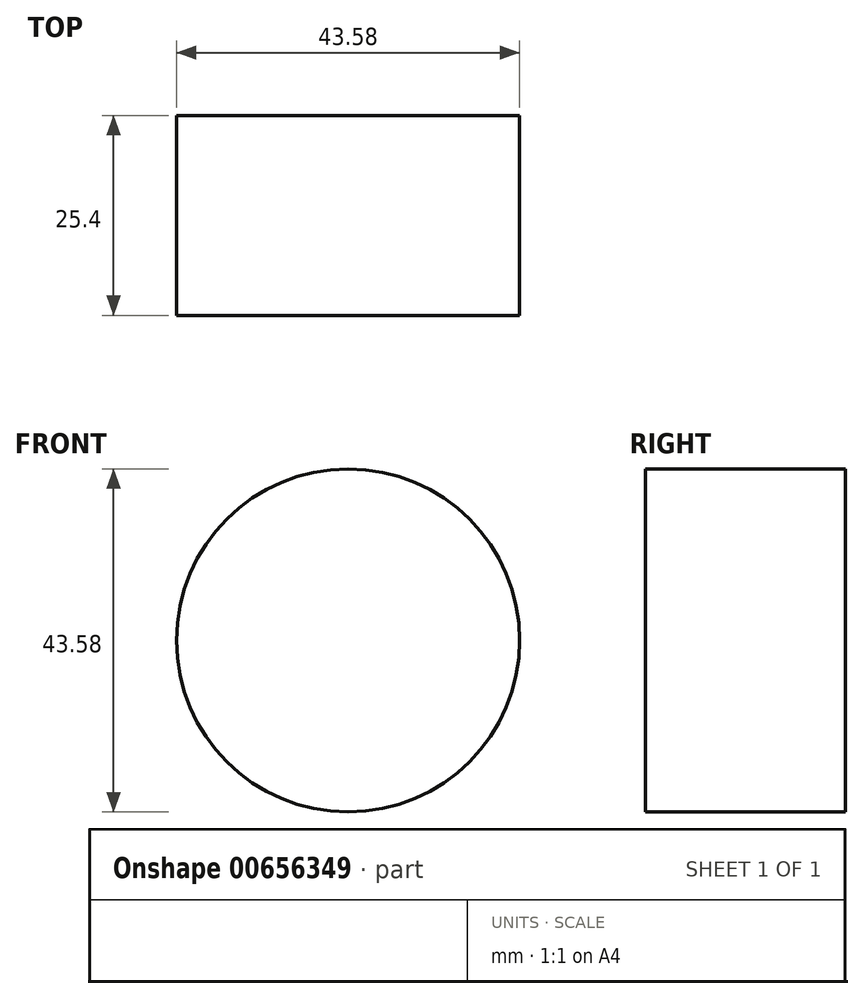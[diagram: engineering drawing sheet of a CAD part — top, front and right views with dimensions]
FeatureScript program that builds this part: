
annotation { "Feature Type Name" : "Feature", "Feature Type Description" : "" }
export const myFeature = defineFeature(function(context is Context, id is Id, definition is map)
    precondition{}
    {
        {
            var Q0;
            Q0=qCreatedBy(makeId("Front.planeOp"),FACE);
            var sketch = newSketch(context, id + "F0", { "sketchPlane" : qUnion([Q0])});
            skCircle(sketch, "E0", {"center": v(0, 0) * mm, "radius": 21.8 * mm});
            skSolve(sketch);
        }
        {
            var Q0;
            Q0=makeQuery(id+"F0.imprint","IMPRINT",FACE,{"disambiguationData":[TD([[makeQuery(id+"F0.imprint","IMPRINT",EDGE,{"derivedFrom":sQuery(id+"F0.wireOp",EDGE,"E0")}),1.0]])]});
            extrude(context, id + "F1", {"entities" : qUnion([Q0]), "depth" : 25.4 * mm, "offsetDistance" : 25.4 * mm});
        }
    });
